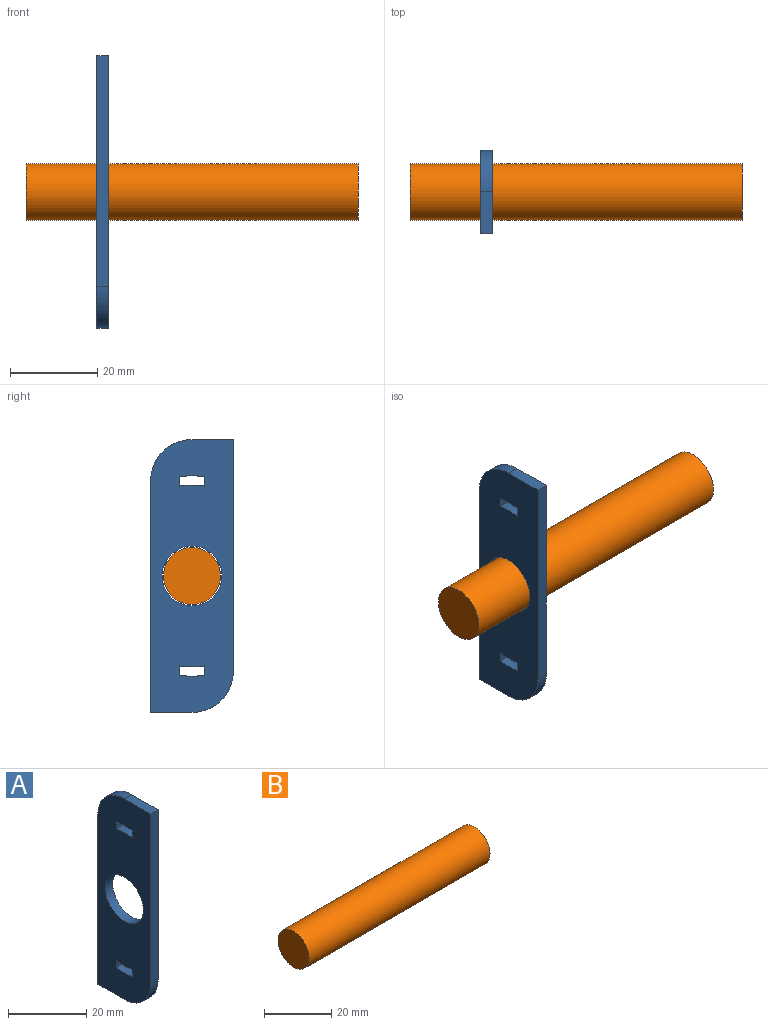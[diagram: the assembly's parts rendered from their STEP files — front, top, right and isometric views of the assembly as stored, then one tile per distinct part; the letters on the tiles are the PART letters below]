
ASSEMBLY  parts=2 mates=2
PART A: 17 faces, bbox 2.7x19.1x62.6 mm
  f0: plane 62.64x19.05mm, normal (1,0,0), area 982.3mm2, adj f2,f3,f4,f5,f6,f7,f8,f9
  f1: plane 62.64x19.05mm, normal (-1,0,0), area 982.3mm2, adj f2,f3,f4,f5,f6,f7,f8,f9
  f2: plane 53.11x2.66mm, normal (0,-1,0), area 141.1mm2, adj f0,f1,f3,f7
  f3: cylinder r=9.53mm len=9.53mm, axis (-1,0,0), area 39.8mm2, adj f0,f1,f2,f4
  f4: plane 9.53x2.66mm, normal (0,0,-1), area 25.3mm2, adj f0,f1,f3,f5
  f5: plane 53.11x2.66mm, normal (0,1,0), area 141.1mm2, adj f0,f1,f4,f6
  f6: cylinder r=9.53mm len=9.53mm, axis (-1,0,0), area 39.8mm2, adj f0,f1,f5,f7
  f7: plane 9.53x2.66mm, normal (0,0,1), area 25.3mm2, adj f0,f1,f2,f6
  f8: cylinder r=6.86mm len=13.72mm, axis (1,0,0), area 114.5mm2, adj f0,f1
  f9: plane 2.66x2.18mm, normal (0,-1,0), area 5.8mm2, adj f0,f1,f10,f12
  f10: cylinder r=22.99mm len=5.59mm, axis (-1,0,0), area 14.9mm2, adj f0,f1,f9,f11
  f11: plane 2.66x2.18mm, normal (0,1,0), area 5.8mm2, adj f0,f1,f10,f12
  f12: cylinder r=20.83mm len=5.59mm, axis (-1,0,0), area 14.9mm2, adj f0,f1,f9,f11
  f13: cylinder r=22.99mm len=5.59mm, axis (-1,0,0), area 14.9mm2, adj f0,f1,f14,f16
  f14: plane 2.66x2.18mm, normal (0,-1,0), area 5.8mm2, adj f0,f1,f13,f15
  f15: cylinder r=20.83mm len=5.59mm, axis (-1,0,0), area 14.9mm2, adj f0,f1,f14,f16
  f16: plane 2.66x2.18mm, normal (0,1,0), area 5.8mm2, adj f0,f1,f13,f15
PART B: 3 faces, bbox 76.2x13.1x13.1 mm
  f0: cylinder r=6.54mm len=76.2mm, axis (-1,0,0), area 3131.5mm2, adj f1,f2
  f1: plane 13.08x13.08mm, normal (1,0,0), area 134.4mm2, adj f0
  f2: plane 13.08x13.08mm, normal (-1,0,0), area 134.4mm2, adj f0
PLACE A t=(8.22,13.22,-5.05)mm
PLACE B t=(-9.36,13.22,-5.05)mm fixed
MATE parallel B.f0 <-> A.f8  axis (-1,0,0) through (-9.36,13.22,-5.05)mm
MATE slider B.f0 <-> A.f8  axis (-1,0,0) through (-9.36,13.22,-5.05)mm
